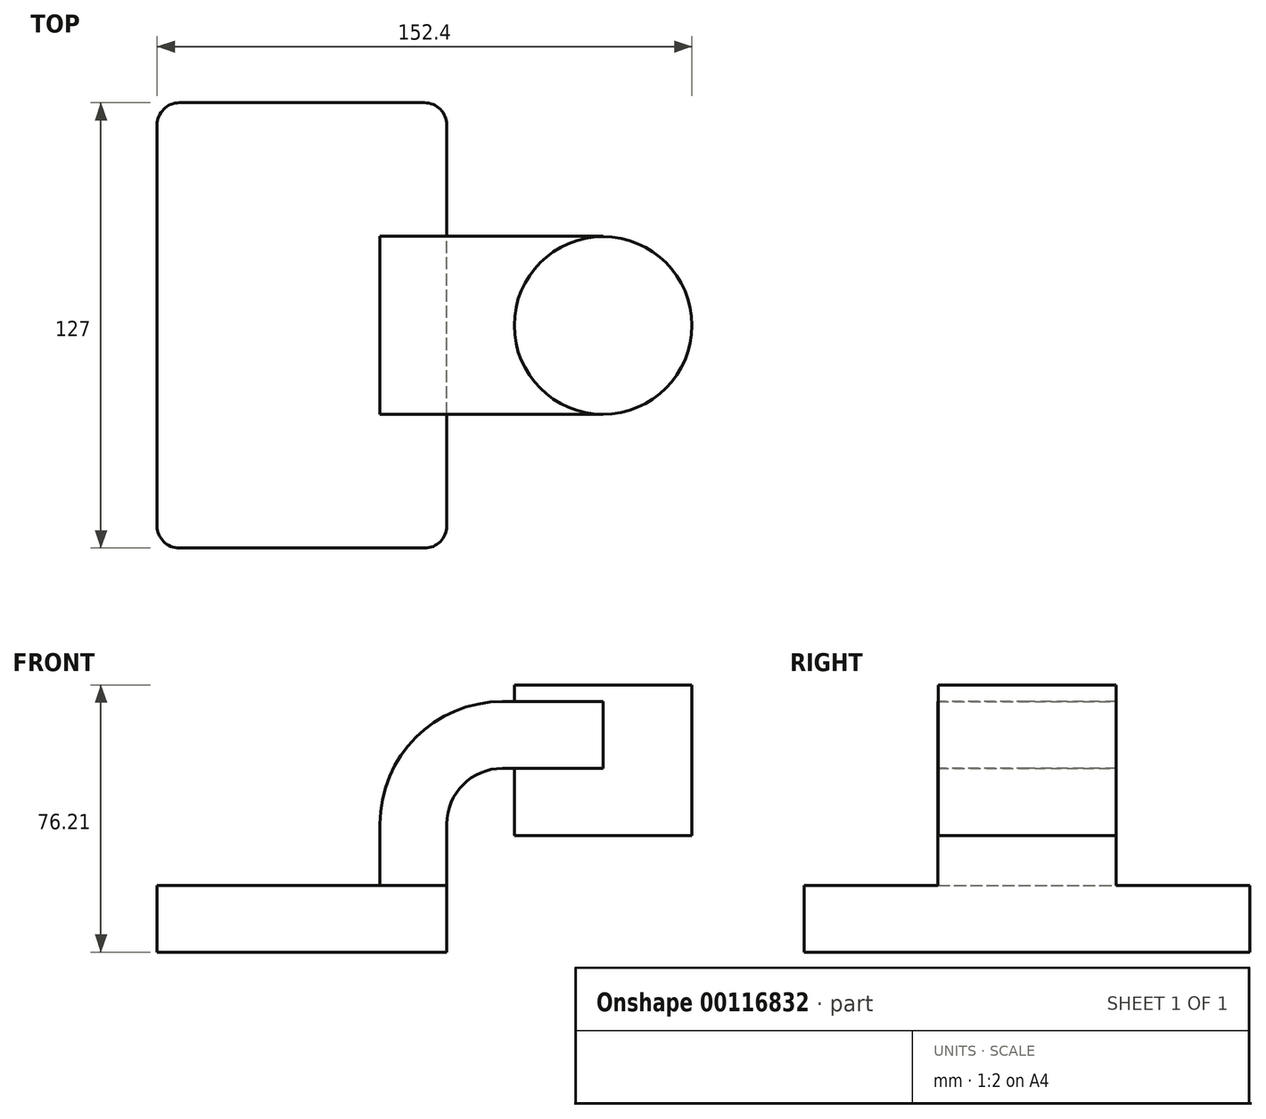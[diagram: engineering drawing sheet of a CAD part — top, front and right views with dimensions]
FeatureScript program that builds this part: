
annotation { "Feature Type Name" : "Feature", "Feature Type Description" : "" }
export const myFeature = defineFeature(function(context is Context, id is Id, definition is map)
    precondition{}
    {
        {
            var Q0;
            Q0=qCreatedBy(makeId("Front.planeOp"),FACE);
            var sketch = newSketch(context, id + "F0", { "sketchPlane" : qUnion([Q0])});
            skLineSegment(sketch, "E0.bottom", {"start": v(-41.28, 9.53) * mm, "end": v(41.28, 9.53) * mm});
            skLineSegment(sketch, "E0.top", {"start": v(-41.28, -9.53) * mm, "end": v(41.28, -9.53) * mm});
            skLineSegment(sketch, "E0.left", {"start": v(-41.28, 9.53) * mm, "end": v(-41.28, -9.53) * mm});
            skLineSegment(sketch, "E0.right", {"start": v(41.28, 9.53) * mm, "end": v(41.28, -9.53) * mm});
            skPoint(sketch, "E0.middle", {"position": v(0, 0) * mm});
            skLineSegment(sketch, "E1.bottom", {"start": v(111.13, 23.68) * mm, "end": v(60.33, 23.68) * mm});
            skLineSegment(sketch, "E1.top", {"start": v(111.13, 66.68) * mm, "end": v(60.33, 66.68) * mm});
            skLineSegment(sketch, "E1.left", {"start": v(111.13, 23.68) * mm, "end": v(111.13, 66.68) * mm});
            skLineSegment(sketch, "E1.right", {"start": v(60.33, 23.68) * mm, "end": v(60.33, 66.68) * mm});
            skPoint(sketch, "E1.middle", {"position": v(85.72, 45.18) * mm});
            skLineSegment(sketch, "E2", {"start": v(41.28, 9.52) * mm, "end": v(41.28, 27) * mm});
            skArc(sketch, "E3", {"start": v(41.27, 27) * mm, "mid": v(45.92, 38.23) * mm, "end": v(57.15, 42.88) * mm});
            skLineSegment(sketch, "E4", {"start": v(57.15, 42.88) * mm, "end": v(85.8, 42.88) * mm});
            skLineSegment(sketch, "E5.0", {"start": v(57.15, 61.93) * mm, "end": v(85.8, 61.93) * mm});
            skArc(sketch, "E5.1", {"start": v(22.23, 27) * mm, "mid": v(32.45, 51.7) * mm, "end": v(57.15, 61.93) * mm});
            skLineSegment(sketch, "E5.2", {"start": v(22.23, 9.52) * mm, "end": v(22.23, 27) * mm});
            skLineSegment(sketch, "E6", {"start": v(85.8, 42.88) * mm, "end": v(85.8, 66.68) * mm});
            skLineSegment(sketch, "E7", {"start": v(85.8, 42.88) * mm, "end": v(85.8, 23.68) * mm});
            skFitSpline(sketch, "E8", {"points": [v(-41.28, 9.53) * mm, v(57.15, 61.93) * mm], "startDerivative": vector(6.67, 107.77) * mm, "endDerivative": vector(103.97, -8.8) * mm});
            skSolve(sketch);
        }
        {
            var Q0;
            Q0=makeQuery(id+"F0.imprint","IMPRINT",FACE,{"disambiguationData":[TD([[makeQuery(id+"F0.imprint","IMPRINT",EDGE,{"derivedFrom":sQuery(id+"F0.wireOp",EDGE,"E0.top")}),1.0]])]});
            extrude(context, id + "F1", {"entities" : qUnion([Q0]), "endBound" : BoundingType.SYMMETRIC, "depth" : 127 * mm});
        }
        {
            var Q0;
            {var subQ1=sQuery(id+"F0.wireOp",EDGE,"E2");Q0=makeQuery(id+"F0.imprint","IMPRINT",FACE,{"disambiguationData":[TD([[makeQuery(id+"F0.imprint","IMPRINT",EDGE,{"derivedFrom":subQ1}),1.0]])]});}
            var Q1;
            {var subQ0=sQuery(id+"F0.wireOp",EDGE,"E4");var subQ1=sQuery(id+"F0.wireOp",EDGE,"E1.right");var subQ2=makeQuery(id+"F0.imprint","INTERSECT",VERTEX,{"derivedFrom":[subQ1,subQ0]});Q1=makeQuery(id+"F0.imprint","IMPRINT",FACE,{"disambiguationData":[TD([[makeQuery(id+"F0.imprint","IMPRINT",EDGE,{"disambiguationData":[TD([[subQ2,-1.0]])],"derivedFrom":subQ1}),-1.0]])]});}
            extrude(context, id + "F2", {"entities" : qUnion([Q0, Q1]), "operationType" : NewBodyOperationType.ADD, "endBound" : BoundingType.SYMMETRIC, "depth" : 50.8 * mm});
        }
        {
            var Q0;
            Q0=makeQuery(id+"F0.imprint","IMPRINT",FACE,{"disambiguationData":[TD([[makeQuery(id+"F0.imprint","IMPRINT",EDGE,{"derivedFrom":sQuery(id+"F0.wireOp",EDGE,"E5.1")}),1.0]])]});
            extrude(context, id + "F3", {"entities" : qUnion([Q0]), "operationType" : NewBodyOperationType.ADD, "endBound" : BoundingType.SYMMETRIC, "depth" : 15.88 * mm});
        }
        {
            var Q0;
            {var subQ0=sQuery(id+"F0.wireOp",EDGE,"E1.left");Q0=makeQuery(id+"F0.imprint","IMPRINT",FACE,{"disambiguationData":[TD([[makeQuery(id+"F0.imprint","IMPRINT",EDGE,{"derivedFrom":subQ0}),1.0]])]});}
            var Q1;
            Q1=sQuery(id+"F0.wireOp",EDGE,"E6");
            revolve(context, id + "F4", {"operationType" : NewBodyOperationType.ADD, "entities" : qUnion([Q0]), "axis" : qUnion([Q1]), "revolveType" : RevolveType.FULL});
        }
        {
            var Q0;
            Q0=makeQuery(id+"F1.opExtrude","CAP_EDGE",EDGE,{"disambiguationData":[OSD([sQuery(id+"F0.wireOp",EDGE,"E0.left")])],"isStart":false});
            var Q1;
            Q1=makeQuery(id+"F1.opExtrude","CAP_EDGE",EDGE,{"disambiguationData":[OSD([sQuery(id+"F0.wireOp",EDGE,"E0.right")])],"isStart":false});
            var Q2;
            Q2=makeQuery(id+"F1.opExtrude","CAP_EDGE",EDGE,{"disambiguationData":[OSD([sQuery(id+"F0.wireOp",EDGE,"E0.right")])],"isStart":true});
            var Q3;
            Q3=makeQuery(id+"F1.opExtrude","CAP_EDGE",EDGE,{"disambiguationData":[OSD([sQuery(id+"F0.wireOp",EDGE,"E0.left")])],"isStart":true});
            fillet(context, id + "F5", {"entities" : qUnion([Q0, Q1, Q2, Q3]), "radius" : 6.35 * mm, "tangentPropagation" : true, "allowEdgeOverflow" : false});
        }
    });
